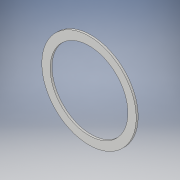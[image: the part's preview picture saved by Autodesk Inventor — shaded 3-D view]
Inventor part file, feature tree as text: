
AUTODESK INVENTOR PART (.ipt)
format: ipt  version: 2019 (Build 230136000, 136)  size: 103,424 bytes
history: native  units: mm
features: extrude x2, sketch x2
ambient origin geometry x8: Origin, YZ Plane, XZ Plane, XY Plane, X Axis, Y Axis, Z Axis, Center Point
bodies: Solid1 (feature_tree)
feature tree (4):
  extrude  "Extrusion1"  Depth=6.0mm TaperAngle=0.0deg
  extrude  "Extrusion2"  Depth=6.0mm TaperAngle=0.0deg
  sketch  "Sketch1"  dims[d0=285.0mm d1=6.0mm d2=0.0mm]
  sketch  "Sketch2"  dims[d3=235.0mm d4=6.0mm d5=0.0mm]
